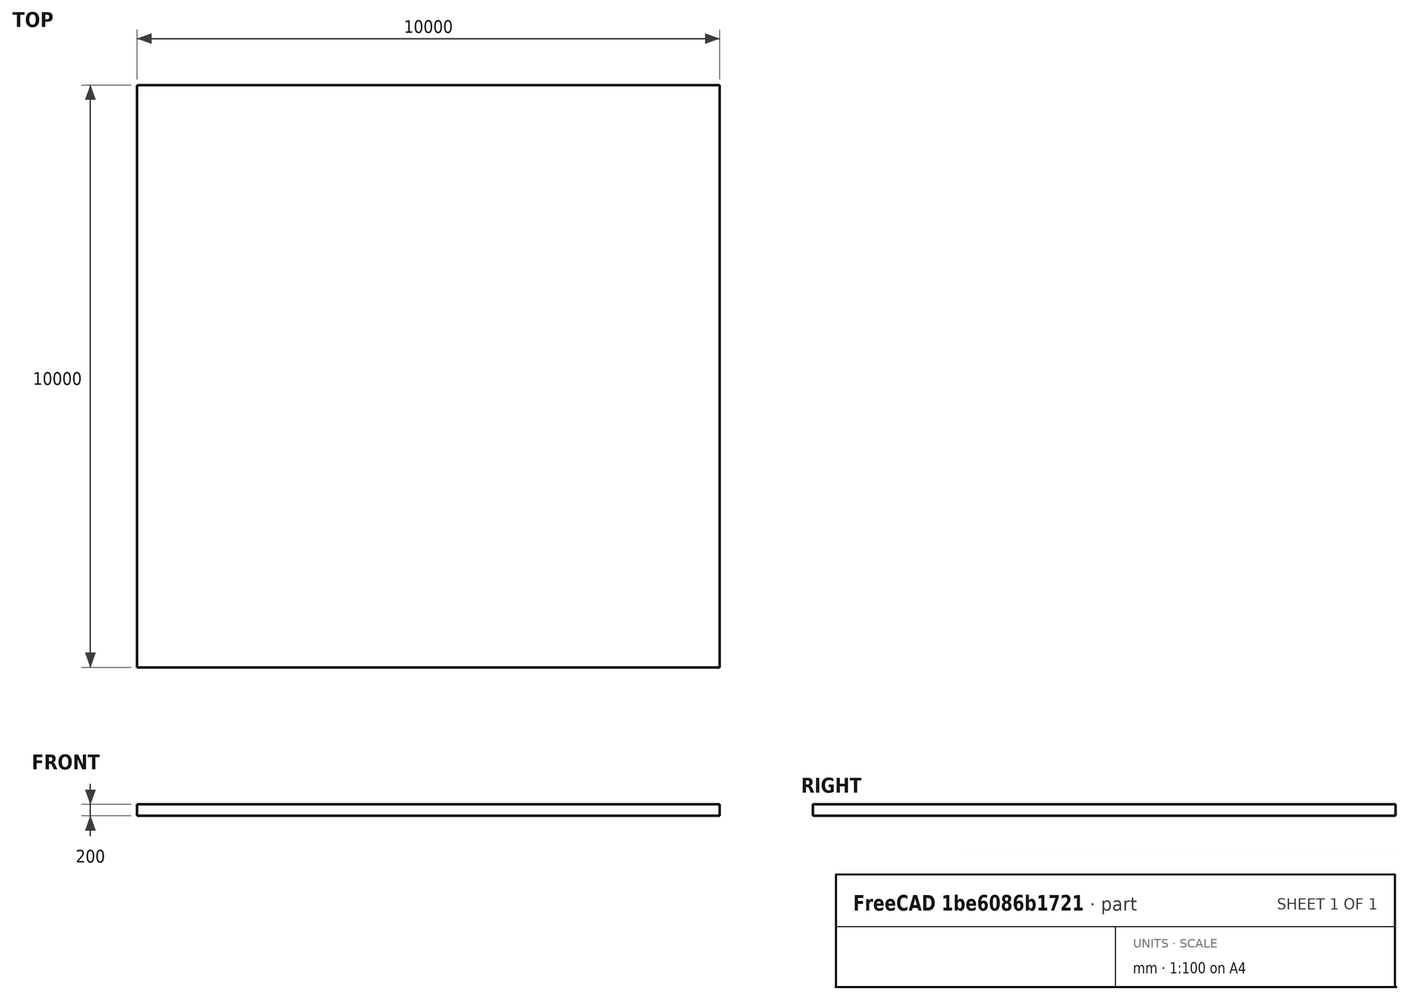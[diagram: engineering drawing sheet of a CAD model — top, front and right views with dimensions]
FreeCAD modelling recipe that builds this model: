
FCSTD DOCUMENT  (FreeCAD 0.21R33694 (Git))
Label: slab
License: All rights reserved
LicenseURL: http://en.wikipedia.org/wiki/All_rights_reserved
objects: Part::Box×1, Fem::ConstraintFixed×1, App::MaterialObjectPython×1, Fem::FemMeshObjectPython×1, Fem::FemSolverObjectPython×1, Fem::ConstraintPressure×1, Fem::FemAnalysis×1
note: 1 computed .brp shape members not serialized (recipe doc carries the construction recipe); baked Part::Feature solids carry a one-line shape summary decoded from their .brp

FEATURE [Part::Box] Box  label="Cube"
  AttacherType = Attacher::AttachEngine3D
  Height = 200
  Length = 10000
  Width = 10000
FEATURE [Fem::ConstraintFixed] ConstraintFixed
  NormalDirection = (0,-1,0)
  Normals = (272) [(0,-1,0),(0,-1,0),(0,-1,0),(0,-1,0),(0,-1,0),(0,-1,0),(0,-1,0),(0,-1,0),(0,-1,0),(0,-1,0),(0,-1,0),(0,-1,0),(0,-1,0),(0,-1,0),(0,-1,0),(0,-1,0),+256 more]
  Points = (272) [(0,0,0),(0,0,66.6667),(0,0,133.333),(0,0,200),(625,0,0),(625,0,66.6667),(625,0,133.333),(625,0,200),(1250,0,0),(1250,0,66.6667),(1250,0,133.333),+261 more]
  References = -> [Box]
  Scale = 62
FEATURE [App::MaterialObjectPython] MaterialSolid  # material (typed FeaturePython)
  Category = 0
  Material = AuthorAndLicense=(c) 2013 Yorik van Havre (CC-BY 3.0),CardName=Concrete-Generic,CompressiveStrength=25 MPa,Density=2400 kg/m^3,+7 more (map truncated)
FEATURE [Fem::FemMeshObjectPython] FEMMeshGmsh  # FEM object (typed FeaturePython)
  Algorithm2D = 0
  Algorithm3D = 0
  CharacteristicLengthMax = 0
  CharacteristicLengthMin = 0
  CoherenceMesh = true
  ElementDimension = 0
  ElementOrder = 1
  GeometryTolerance = 1e-06
  GroupsOfNodes = false
  HighOrderOptimize = 0
  MeshSizeFromCurvature = 12
  OptimizeNetgen = false
  OptimizeStd = true
  Part = -> Box
  RecombinationAlgorithm = 0
  Recombine3DAll = false
  RecombineAll = false
  SecondOrderLinear = false
FEATURE [Fem::FemSolverObjectPython] SolverCcxTools  # FEM object (typed FeaturePython)
  AnalysisType = 0
  BeamShellResultOutput3D = false
  BucklingFactors = 1
  EigenmodeHighLimit = 1000000
  EigenmodeLowLimit = 0
  EigenmodesCount = 10
  GeometricalNonlinearity = 0
  IterationsControlParameterCutb = 0.25,0.5,0.75,0.85,,,1.5,
  IterationsControlParameterIter = 4,8,9,200,10,400,,200,,
  IterationsControlParameterTimeUse = false
  IterationsThermoMechMaximum = 2000
  IterationsUserDefinedIncrementations = false
  IterationsUserDefinedTimeStepLength = false
  MaterialNonlinearity = 0
  MatrixSolverType = 0
  SplitInputWriter = false
  ThermoMechSteadyState = true
  TimeEnd = 1
  TimeInitialStep = 0.01
FEATURE [Fem::ConstraintPressure] ConstraintPressure
  NormalDirection = (0,0,1)
  Normals = (196) [(0,0,1),(0,0,1),(0,0,1),(0,0,1),(0,0,1),(0,0,1),(0,0,1),(0,0,1),(0,0,1),(0,0,1),(0,0,1),(0,0,1),(0,0,1),(0,0,1),(0,0,1),(0,0,1),(0,0,1),(0,0,1),+178 more]
  Points = (196) [(0,0,200),(769.231,0,200),(1538.46,0,200),(2307.69,0,200),(3076.92,0,200),(3846.15,0,200),(4615.38,0,200),(5384.62,0,200),(6153.85,0,200),+187 more]
  Pressure = 0.1
  References = -> [Box]
  Scale = 78
FEATURE [Fem::FemAnalysis] Analysis
  Group = -> [ConstraintFixed,MaterialSolid,FEMMeshGmsh,SolverCcxTools,ConstraintPressure]
